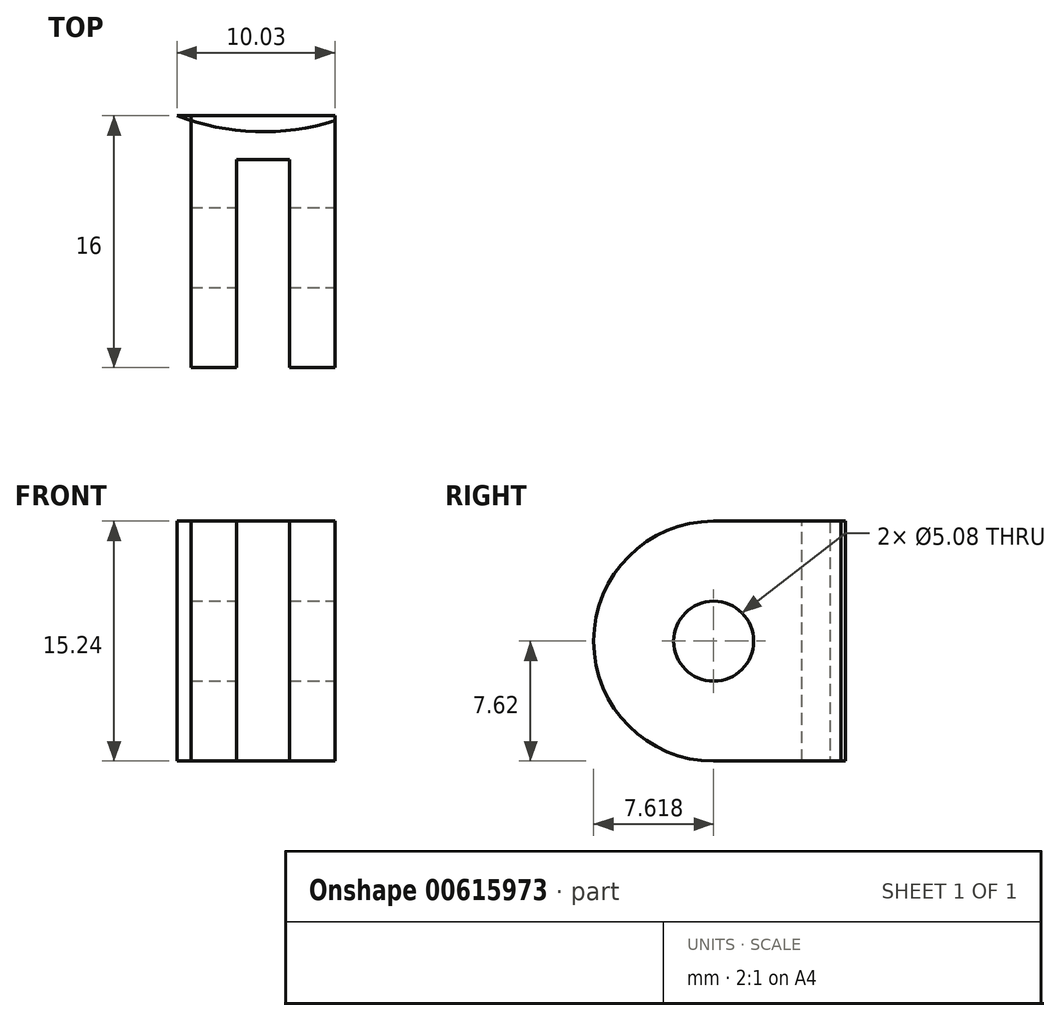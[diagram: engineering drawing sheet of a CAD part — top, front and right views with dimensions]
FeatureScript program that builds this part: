
annotation { "Feature Type Name" : "Feature", "Feature Type Description" : "" }
export const myFeature = defineFeature(function(context is Context, id is Id, definition is map)
    precondition{}
    {
        {
            var Q0;
            Q0=qCreatedBy(makeId("Top.planeOp"),FACE);
            var sketch = newSketch(context, id + "F0", { "sketchPlane" : qUnion([Q0])});
            skCircle(sketch, "E0", {"center": v(0, 0) * mm, "radius": 12.7 * mm});
            skCircle(sketch, "E1", {"center": v(0, 0) * mm, "radius": 15.24 * mm});
            skSolve(sketch);
        }
        {
            var Q0;
            Q0=qSketchRegion(id+"F0",true);
            extrude(context, id + "F1", {"entities" : qUnion([Q0]), "depth" : 15.24 * mm});
        }
        {
            var Q0;
            Q0=makeQuery(id+"F1.opExtrude","CAP_FACE",FACE,{"disambiguationData":[OSD([sQuery(id+"F0.wireOp",EDGE,"E0"),sQuery(id+"F0.wireOp",EDGE,"E1")])],"isStart":false});
            var sketch = newSketch(context, id + "F2", { "sketchPlane" : qUnion([Q0])});
            skLineSegment(sketch, "E2", {"start": v(-3.18, 0) * mm, "end": v(-3.18, 31.75) * mm});
            skLineSegment(sketch, "E3", {"start": v(-3.18, 31.75) * mm, "end": v(3.17, 31.75) * mm});
            skLineSegment(sketch, "E4", {"start": v(3.18, 31.75) * mm, "end": v(3.18, 0) * mm});
            skLineSegment(sketch, "E5", {"start": v(3.18, 0) * mm, "end": v(0, 0) * mm});
            skLineSegment(sketch, "E6", {"start": v(0, 0) * mm, "end": v(-3.18, 0) * mm});
            skSolve(sketch);
        }
        {
            var Q0;
            Q0=qSketchRegion(id+"F2",true);
            extrude(context, id + "F3", {"entities" : qUnion([Q0]), "operationType" : NewBodyOperationType.REMOVE, "oppositeDirection" : true, "depth" : 25.4 * mm});
        }
        {
            var Q0;
            Q0=makeQuery(id+"F3.boolean.opBoolean","COPY",FACE,{"derivedFrom":makeQuery(id+"F3.opExtrude","SWEPT_FACE",FACE,{"disambiguationData":[OSD([sQuery(id+"F2.wireOp",EDGE,"E2")])]})});
            var sketch = newSketch(context, id + "F4", { "sketchPlane" : qUnion([Q0])});
            skLineSegment(sketch, "E7.bottom", {"start": v(12.3, 15.24) * mm, "end": v(19.92, 15.24) * mm});
            skLineSegment(sketch, "E7.top", {"start": v(12.3, 0) * mm, "end": v(19.92, 0) * mm});
            skLineSegment(sketch, "E7.left", {"start": v(12.3, 15.24) * mm, "end": v(12.3, 0) * mm});
            skLineSegment(sketch, "E7.right", {"start": v(19.92, 15.24) * mm, "end": v(19.92, 0) * mm});
            skArc(sketch, "E8", {"start": v(19.92, 0) * mm, "mid": v(27.54, 7.62) * mm, "end": v(19.92, 15.24) * mm});
            skSolve(sketch);
        }
        {
            var Q0;
            Q0=qSketchRegion(id+"F4",true);
            extrude(context, id + "F5", {"entities" : qUnion([Q0]), "operationType" : NewBodyOperationType.ADD, "oppositeDirection" : true, "depth" : 3.8 * mm});
        }
        {
            var Q0;
            Q0=makeQuery(id+"F3.boolean.opBoolean","COPY",FACE,{"derivedFrom":makeQuery(id+"F3.opExtrude","SWEPT_FACE",FACE,{"disambiguationData":[OSD([sQuery(id+"F2.wireOp",EDGE,"E4")])]})});
            var sketch = newSketch(context, id + "F6", { "sketchPlane" : qUnion([Q0])});
            skLineSegment(sketch, "E9.bottom", {"start": v(-12.3, 15.24) * mm, "end": v(-19.92, 15.24) * mm});
            skLineSegment(sketch, "E9.top", {"start": v(-12.3, 0) * mm, "end": v(-19.92, 0) * mm});
            skLineSegment(sketch, "E9.left", {"start": v(-12.3, 15.24) * mm, "end": v(-12.3, 0) * mm});
            skLineSegment(sketch, "E9.right", {"start": v(-19.92, 15.24) * mm, "end": v(-19.92, 0) * mm});
            skArc(sketch, "E10", {"start": v(-19.92, 15.24) * mm, "mid": v(-27.54, 7.62) * mm, "end": v(-19.92, 0) * mm});
            skSolve(sketch);
        }
        {
            var Q0;
            Q0=qSketchRegion(id+"F6",true);
            extrude(context, id + "F7", {"entities" : qUnion([Q0]), "operationType" : NewBodyOperationType.ADD, "oppositeDirection" : true, "depth" : 3.8 * mm});
        }
        {
            var Q0;
            Q0=makeQuery(id+"F5.opExtrude","CAP_FACE",FACE,{"disambiguationData":[OSD([sQuery(id+"F4.wireOp",EDGE,"E7.bottom"),sQuery(id+"F4.wireOp",EDGE,"E7.top"),sQuery(id+"F4.wireOp",EDGE,"E7.left"),sQuery(id+"F4.wireOp",EDGE,"E8")])],"isStart":false});
            var sketch = newSketch(context, id + "F8", { "sketchPlane" : qUnion([Q0])});
            skCircle(sketch, "E11", {"center": v(-19.06, 7.62) * mm, "radius": 2.54 * mm});
            skPoint(sketch, "E11.centerSnap0", {"position": v(-13.55, 7.62) * mm});
            skSolve(sketch);
        }
        {
            var Q0;
            Q0=qSketchRegion(id+"F8",true);
            extrude(context, id + "F9", {"entities" : qUnion([Q0]), "operationType" : NewBodyOperationType.REMOVE, "oppositeDirection" : true, "depth" : 25.4 * mm});
        }
        {
            var Q0;
            Q0=makeQuery(id+"F5.opExtrude","CAP_FACE",FACE,{"disambiguationData":[OSD([sQuery(id+"F4.wireOp",EDGE,"E7.bottom"),sQuery(id+"F4.wireOp",EDGE,"E7.top"),sQuery(id+"F4.wireOp",EDGE,"E7.left"),sQuery(id+"F4.wireOp",EDGE,"E8")])],"isStart":false});
            var sketch = newSketch(context, id + "F10", { "sketchPlane" : qUnion([Q0])});
            skCircle(sketch, "E12", {"center": v(-19.06, 7.62) * mm, "radius": 5.33 * mm});
            skCircle(sketch, "E13.cCircle", {"center": v(-19.06, 7.62) * mm, "radius": 3.94 * mm, "construction": true});
            skLineSegment(sketch, "E13.0", {"start": v(-23, 5.35) * mm, "end": v(-23, 9.9) * mm});
            skLineSegment(sketch, "E13.1", {"start": v(-23, 9.9) * mm, "end": v(-19.06, 12.17) * mm});
            skLineSegment(sketch, "E13.2", {"start": v(-19.06, 12.17) * mm, "end": v(-15.12, 9.9) * mm});
            skLineSegment(sketch, "E13.3", {"start": v(-15.12, 9.9) * mm, "end": v(-15.12, 5.35) * mm});
            skLineSegment(sketch, "E13.4", {"start": v(-15.12, 5.35) * mm, "end": v(-19.06, 3.07) * mm});
            skLineSegment(sketch, "E13.5", {"start": v(-19.06, 3.07) * mm, "end": v(-23, 5.35) * mm});
            skPoint(sketch, "E13.0.midPoint", {"position": v(-23, 7.62) * mm});
            skSolve(sketch);
        }
        {
            var Q0;
            Q0=qSketchRegion(id+"F10",true);
            extrude(context, id + "F11", {"entities" : qUnion([Q0]), "operationType" : NewBodyOperationType.ADD, "depth" : 1.9 * mm});
        }
        {
            var Q0;
            {var subQ0=sQuery(id+"F4.wireOp",EDGE,"E8");var subQ1=sQuery(id+"F4.wireOp",EDGE,"E7.left");var subQ2=sQuery(id+"F4.wireOp",EDGE,"E7.top");var subQ3=sQuery(id+"F4.wireOp",EDGE,"E7.bottom");var subQ4=makeQuery(id+"F5.opExtrude","CAP_FACE",FACE,{"disambiguationData":[OSD([subQ3,subQ2,subQ1,subQ0])],"isStart":false});Q0=makeQuery(id+"F11.boolean.opBoolean","SPLIT",FACE,{"disambiguationData":[TD([makeQuery(id+"F11.opExtrude","SWEPT_FACE",FACE,{"disambiguationData":[OSD([sQuery(id+"F10.wireOp",EDGE,"E13.0")])]})])],"derivedFrom":subQ4});}
            extrude(context, id + "F12", {"entities" : qUnion([Q0]), "operationType" : NewBodyOperationType.REMOVE, "oppositeDirection" : true, "depth" : 1.9 * mm});
        }
        {
            var Q0;
            Q0=makeQuery(id+"F7.boolean.opBoolean","MERGE",FACE,{"derivedFrom":[makeQuery(id+"F5.boolean.opBoolean","MERGE",FACE,{"derivedFrom":[makeQuery(id+"F1.opExtrude","CAP_FACE",FACE,{"disambiguationData":[OSD([sQuery(id+"F0.wireOp",EDGE,"E0"),sQuery(id+"F0.wireOp",EDGE,"E1")])],"isStart":false}),makeQuery(id+"F5.opExtrude","SWEPT_FACE",FACE,{"disambiguationData":[OSD([sQuery(id+"F4.wireOp",EDGE,"E7.bottom")])]})]}),makeQuery(id+"F7.opExtrude","SWEPT_FACE",FACE,{"disambiguationData":[OSD([sQuery(id+"F6.wireOp",EDGE,"E9.bottom")])]})]});
            var sketch = newSketch(context, id + "F13", { "sketchPlane" : qUnion([Q0])});
            skLineSegment(sketch, "E14", {"start": v(0, -12.7) * mm, "end": v(4.57, -12.7) * mm});
            skLineSegment(sketch, "E15", {"start": v(4.57, -12.7) * mm, "end": v(4.57, -32.26) * mm});
            skLineSegment(sketch, "E16", {"start": v(4.57, -32.26) * mm, "end": v(1.69, -32.26) * mm});
            skLineSegment(sketch, "E17", {"start": v(1.69, -32.26) * mm, "end": v(1.69, -17.02) * mm});
            skLineSegment(sketch, "E18", {"start": v(1.69, -17.02) * mm, "end": v(-1.69, -17.02) * mm});
            skLineSegment(sketch, "E19", {"start": v(-1.69, -17.02) * mm, "end": v(-1.69, -32.26) * mm});
            skLineSegment(sketch, "E20", {"start": v(-1.69, -32.26) * mm, "end": v(-4.57, -32.26) * mm});
            skLineSegment(sketch, "E21", {"start": v(-4.57, -32.26) * mm, "end": v(-4.57, -12.7) * mm});
            skLineSegment(sketch, "E22", {"start": v(-4.57, -12.7) * mm, "end": v(0, -12.7) * mm});
            skSolve(sketch);
        }
        {
            var Q0;
            Q0=qSketchRegion(id+"F13",true);
            extrude(context, id + "F14", {"entities" : qUnion([Q0]), "oppositeDirection" : true, "depth" : 15.24 * mm});
        }
        {
            var Q0;
            Q0=makeQuery(id+"F14.opExtrude","SWEPT_FACE",FACE,{"disambiguationData":[OSD([sQuery(id+"F13.wireOp",EDGE,"E15")])]});
            var sketch = newSketch(context, id + "F15", { "sketchPlane" : qUnion([Q0])});
            skLineSegment(sketch, "E23.bottom", {"start": v(-14.23, 15.24) * mm, "end": v(-22.61, 15.24) * mm});
            skLineSegment(sketch, "E23.top", {"start": v(-14.23, 0) * mm, "end": v(-22.61, 0) * mm});
            skLineSegment(sketch, "E23.left", {"start": v(-14.23, 15.24) * mm, "end": v(-14.23, 0) * mm});
            skLineSegment(sketch, "E23.right", {"start": v(-22.61, 15.24) * mm, "end": v(-22.61, 0) * mm});
            skArc(sketch, "E24", {"start": v(-22.61, 15.24) * mm, "mid": v(-30.23, 7.62) * mm, "end": v(-22.61, 0) * mm});
            skCircle(sketch, "E25", {"center": v(-22.61, 7.62) * mm, "radius": 2.54 * mm});
            skSolve(sketch);
        }
        {
            var Q0;
            Q0=qSketchRegion(id+"F15",true);
            extrude(context, id + "F16", {"entities" : qUnion([Q0]), "operationType" : NewBodyOperationType.INTERSECT, "oppositeDirection" : true, "depth" : 25.4 * mm});
        }
    });
